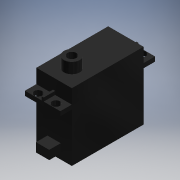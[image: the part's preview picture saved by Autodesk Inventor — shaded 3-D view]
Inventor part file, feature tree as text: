
AUTODESK INVENTOR PART (.ipt)
format: ipt  version: 2017 (Build 210142000, 142)  size: 169,984 bytes
history: native  units: mm (DEFAULTED — no unit token found)
features: extrude x7, sketch x7
ambient origin geometry x8: Origin, YZ Plane, XZ Plane, XY Plane, X Axis, Y Axis, Z Axis, Center Point
bodies: Solid1 (feature_tree)
feature tree (14):
  extrude  "Extrusion1"  Depth=47.0mm TaperAngle=0.0deg
  extrude  "Extrusion2"  Depth=6.5mm TaperAngle=0.0deg
  extrude  "Extrusion3"  Depth=1.2mm
  extrude  "Extrusion4"  TaperAngle=0.0deg  [1 undecoded]
  extrude  "Extrusion5"  Depth=12.0mm TaperAngle=0.0deg
  extrude  "Extrusion6"  [1 undecoded]
  extrude  "Extrusion8"  [1 undecoded]
  sketch  "Sketch1"  dims[d3=0.0mm d7=47.0mm d8=0.0mm d9=0.0mm]
  sketch  "Sketch2"  dims[d13=2.5mm d19=6.5mm d20=0.0mm]
  sketch  "Sketch3"  dims[d24=6.5mm d25=0.0mm d27=1.2mm]
  sketch  "Sketch4"  dims[d28=6.5mm d29=0.0mm d33=0.0mm]
  sketch  "Sketch5"  dims[d39=5.0mm d40=12.0mm d41=0.0mm]
  sketch  "Sketch6"  dims[d42=2.75mm]
  sketch  "Sketch8"
note: 3 required parameter values undecoded (feature->parameter linkage not recoverable at this tier; creation-order binding heuristic only, values carry confidence <= 0.55)
